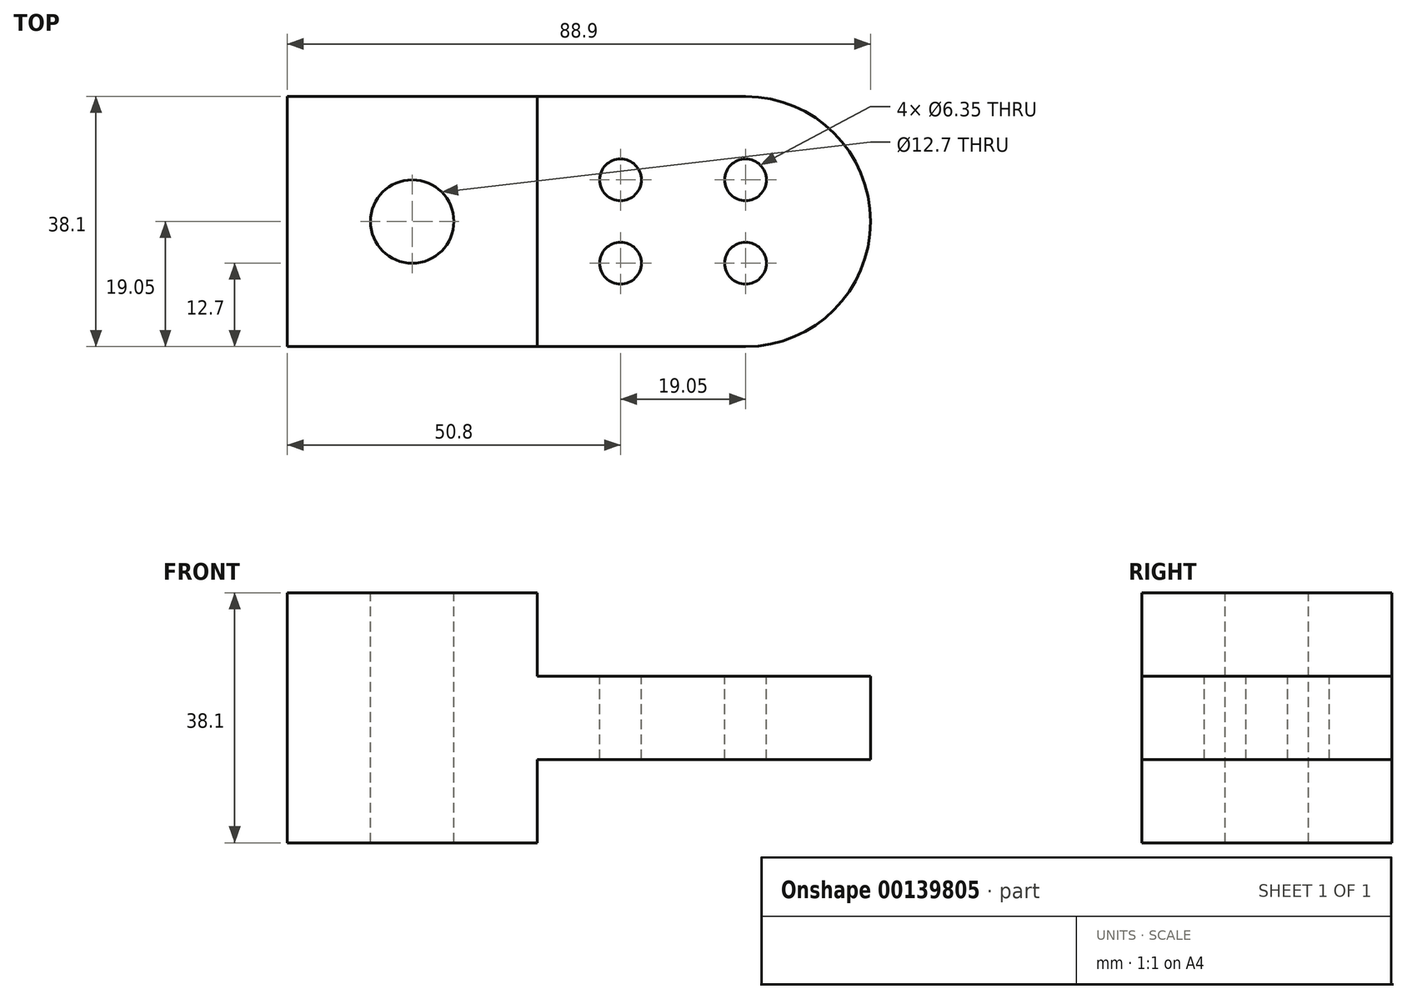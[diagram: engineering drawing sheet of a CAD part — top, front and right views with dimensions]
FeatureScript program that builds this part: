
annotation { "Feature Type Name" : "Feature", "Feature Type Description" : "" }
export const myFeature = defineFeature(function(context is Context, id is Id, definition is map)
    precondition{}
    {
        {
            var Q0;
            Q0=qCreatedBy(makeId("Front.planeOp"),FACE);
            var sketch = newSketch(context, id + "F0", { "sketchPlane" : qUnion([Q0])});
            skLineSegment(sketch, "E0", {"start": v(0, 0) * mm, "end": v(0, 38.1) * mm});
            skLineSegment(sketch, "E1", {"start": v(0, 38.1) * mm, "end": v(38.1, 38.1) * mm});
            skLineSegment(sketch, "E2", {"start": v(38.1, 38.1) * mm, "end": v(38.1, 25.4) * mm});
            skLineSegment(sketch, "E3", {"start": v(38.1, 25.4) * mm, "end": v(88.9, 25.4) * mm});
            skLineSegment(sketch, "E4", {"start": v(88.9, 25.4) * mm, "end": v(88.9, 12.7) * mm});
            skLineSegment(sketch, "E5", {"start": v(88.9, 12.7) * mm, "end": v(38.1, 12.7) * mm});
            skLineSegment(sketch, "E6", {"start": v(38.1, 12.7) * mm, "end": v(38.1, 0) * mm});
            skLineSegment(sketch, "E7", {"start": v(38.1, 0) * mm, "end": v(0, 0) * mm});
            skSolve(sketch);
        }
        {
            var Q0;
            Q0=makeQuery(id+"F0.imprint","IMPRINT",FACE,{"disambiguationData":[TD([[makeQuery(id+"F0.imprint","IMPRINT",EDGE,{"derivedFrom":sQuery(id+"F0.wireOp",EDGE,"E0")}),-1.0]])]});
            extrude(context, id + "F1", {"entities" : qUnion([Q0]), "oppositeDirection" : true, "depth" : 38.1 * mm});
        }
        {
            var Q0;
            Q0=makeQuery(id+"F1.opExtrude","SWEPT_FACE",FACE,{"disambiguationData":[OSD([sQuery(id+"F0.wireOp",EDGE,"E3")])]});
            var sketch = newSketch(context, id + "F2", { "sketchPlane" : qUnion([Q0])});
            skLineSegment(sketch, "E8.bottom", {"start": v(0, 0) * mm, "end": v(38.1, 0) * mm});
            skLineSegment(sketch, "E8.top", {"start": v(0, 38.1) * mm, "end": v(38.1, 38.1) * mm});
            skLineSegment(sketch, "E8.left", {"start": v(0, 0) * mm, "end": v(0, 38.1) * mm});
            skLineSegment(sketch, "E8.right", {"start": v(38.1, 0) * mm, "end": v(38.1, 38.1) * mm});
            skLineSegment(sketch, "E9.bottom", {"start": v(38.1, 0) * mm, "end": v(69.85, 0) * mm});
            skLineSegment(sketch, "E9.top", {"start": v(38.1, 38.1) * mm, "end": v(69.85, 38.1) * mm});
            skLineSegment(sketch, "E9.right", {"start": v(88.9, 19.05) * mm, "end": v(88.9, 19.05) * mm});
            skPoint(sketch, "E10.centerSnap0", {"position": v(19.05, 38.1) * mm});
            skPoint(sketch, "E10.centerSnap1", {"position": v(38.1, 19.05) * mm});
            skPoint(sketch, "E11.visualSharp", {"position": v(88.9, 38.1) * mm});
            skArc(sketch, "E11.filletArc", {"start": v(88.9, 19.05) * mm, "mid": v(83.32, 32.52) * mm, "end": v(69.85, 38.1) * mm});
            skPoint(sketch, "E12.visualSharp", {"position": v(88.9, 0) * mm});
            skArc(sketch, "E12.filletArc", {"start": v(69.85, 0) * mm, "mid": v(83.32, 5.58) * mm, "end": v(88.9, 19.05) * mm});
            skCircle(sketch, "E13", {"center": v(69.85, 25.4) * mm, "radius": 3.18 * mm});
            skCircle(sketch, "E14.0.1.0", {"center": v(69.85, 12.7) * mm, "radius": 3.18 * mm});
            skCircle(sketch, "E14.1.0.0", {"center": v(50.8, 25.4) * mm, "radius": 3.18 * mm});
            skCircle(sketch, "E14.1.1.0", {"center": v(50.8, 12.7) * mm, "radius": 3.18 * mm});
            skLineSegment(sketch, "E14.direction1", {"start": v(69.85, 25.4) * mm, "end": v(50.8, 25.4) * mm, "construction": true});
            skLineSegment(sketch, "E14.direction2", {"start": v(69.85, 25.4) * mm, "end": v(69.85, 12.7) * mm, "construction": true});
            skPoint(sketch, "E10.center.orphan", {"position": v(19.05, 19.05) * mm});
            skSolve(sketch);
        }
        {
            var Q0;
            Q0=makeQuery(id+"F2.imprint","IMPRINT",FACE,{"disambiguationData":[TD([[makeQuery(id+"F2.imprint","IMPRINT",EDGE,{"derivedFrom":sQuery(id+"F2.wireOp",EDGE,"E14.1.0.0")}),1.0]])]});
            var Q1;
            {var subQ0=sQuery(id+"F2.wireOp",EDGE,"E11.filletArc");Q1=makeQuery(id+"F2.imprint","IMPRINT",FACE,{"disambiguationData":[TD([[makeQuery(id+"F2.imprint","IMPRINT",EDGE,{"derivedFrom":subQ0}),-1.0]])]});}
            var Q2;
            {var subQ0=sQuery(id+"F2.wireOp",EDGE,"E12.filletArc");Q2=makeQuery(id+"F2.imprint","IMPRINT",FACE,{"disambiguationData":[TD([[makeQuery(id+"F2.imprint","IMPRINT",EDGE,{"derivedFrom":subQ0}),-1.0]])]});}
            var Q3;
            Q3=makeQuery(id+"F2.imprint","IMPRINT",FACE,{"disambiguationData":[TD([[makeQuery(id+"F2.imprint","IMPRINT",EDGE,{"derivedFrom":sQuery(id+"F2.wireOp",EDGE,"E13")}),1.0]])]});
            var Q4;
            Q4=makeQuery(id+"F2.imprint","IMPRINT",FACE,{"disambiguationData":[TD([[makeQuery(id+"F2.imprint","IMPRINT",EDGE,{"derivedFrom":sQuery(id+"F2.wireOp",EDGE,"E14.0.1.0")}),1.0]])]});
            var Q5;
            Q5=makeQuery(id+"F2.imprint","IMPRINT",FACE,{"disambiguationData":[TD([[makeQuery(id+"F2.imprint","IMPRINT",EDGE,{"derivedFrom":sQuery(id+"F2.wireOp",EDGE,"E14.1.1.0")}),1.0]])]});
            extrude(context, id + "F3", {"entities" : qUnion([Q0, Q1, Q2, Q3, Q4, Q5]), "operationType" : NewBodyOperationType.REMOVE, "endBound" : BoundingType.THROUGH_ALL, "oppositeDirection" : true, "depth" : 25.4 * mm});
        }
        {
            var Q0;
            Q0=makeQuery(id+"F1.opExtrude","SWEPT_FACE",FACE,{"disambiguationData":[OSD([sQuery(id+"F0.wireOp",EDGE,"E1")])]});
            var sketch = newSketch(context, id + "F4", { "sketchPlane" : qUnion([Q0])});
            skCircle(sketch, "E15", {"center": v(19.05, 19.05) * mm, "radius": 6.35 * mm});
            skPoint(sketch, "E15.centerSnap0", {"position": v(38.1, 19.05) * mm});
            skPoint(sketch, "E15.centerSnap1", {"position": v(19.05, 38.1) * mm});
            skSolve(sketch);
        }
        {
            var Q0;
            Q0=makeQuery(id+"F4.imprint","IMPRINT",FACE,{"disambiguationData":[TD([[makeQuery(id+"F4.imprint","IMPRINT",EDGE,{"derivedFrom":sQuery(id+"F4.wireOp",EDGE,"E15")}),1.0]])]});
            extrude(context, id + "F5", {"entities" : qUnion([Q0]), "operationType" : NewBodyOperationType.REMOVE, "endBound" : BoundingType.THROUGH_ALL, "oppositeDirection" : true, "depth" : 25.4 * mm});
        }
    });
